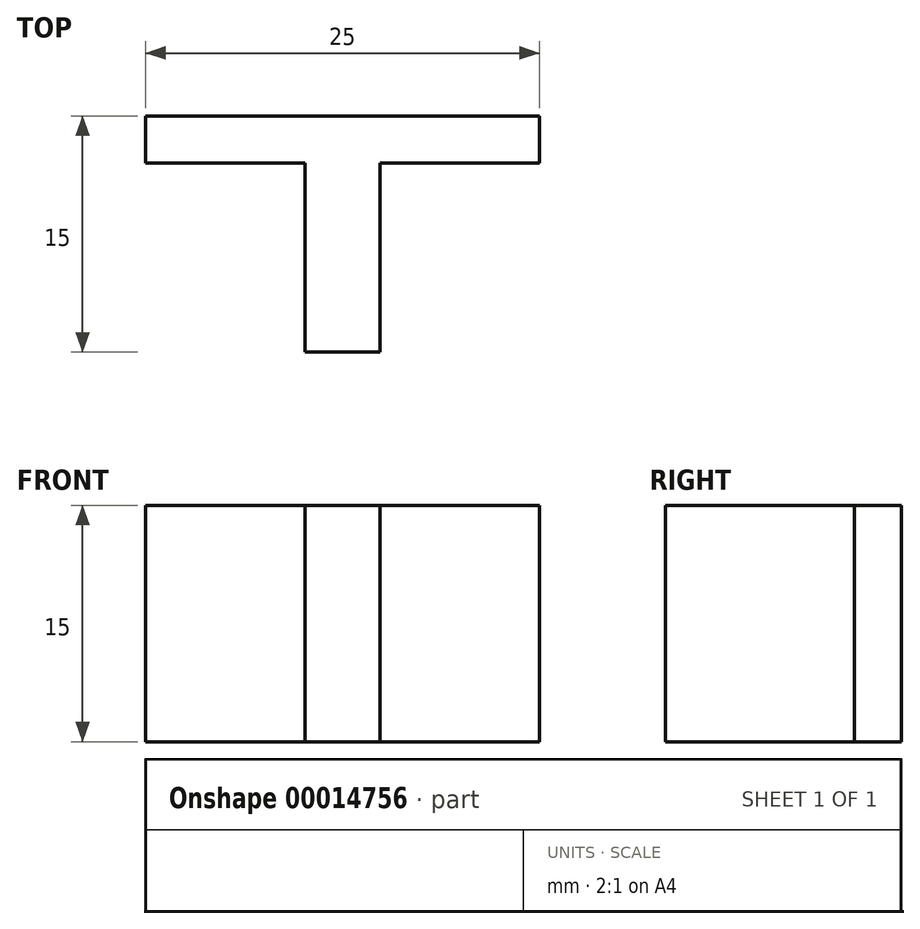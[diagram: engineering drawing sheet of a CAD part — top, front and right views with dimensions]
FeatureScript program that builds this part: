
annotation { "Feature Type Name" : "Feature", "Feature Type Description" : "" }
export const myFeature = defineFeature(function(context is Context, id is Id, definition is map)
    precondition{}
    {
        {
            var Q0;
            Q0=qCreatedBy(makeId("Top.planeOp"),FACE);
            var sketch = newSketch(context, id + "F0", { "sketchPlane" : qUnion([Q0])});
            skLineSegment(sketch, "E0", {"start": v(-12.5, 0) * mm, "end": v(-12.5, 3) * mm});
            skLineSegment(sketch, "E1", {"start": v(-12.5, 3) * mm, "end": v(12.5, 3) * mm});
            skLineSegment(sketch, "E2", {"start": v(12.5, 3) * mm, "end": v(12.5, 0) * mm});
            skLineSegment(sketch, "E3", {"start": v(12.5, 0) * mm, "end": v(2.38, 0) * mm});
            skLineSegment(sketch, "E4", {"start": v(2.37, 0) * mm, "end": v(2.38, -12) * mm});
            skLineSegment(sketch, "E5", {"start": v(2.38, -12) * mm, "end": v(-2.37, -12) * mm});
            skLineSegment(sketch, "E6", {"start": v(-2.37, -12) * mm, "end": v(-2.38, 0) * mm});
            skLineSegment(sketch, "E7", {"start": v(-2.38, 0) * mm, "end": v(-12.5, 0) * mm});
            skSolve(sketch);
        }
        {
            var Q0;
            Q0=makeQuery(id+"F0.imprint","IMPRINT",FACE,{"disambiguationData":[TD([[makeQuery(id+"F0.imprint","IMPRINT",EDGE,{"derivedFrom":sQuery(id+"F0.wireOp",EDGE,"E0")}),-1.0]])]});
            extrude(context, id + "F1", {"entities" : qUnion([Q0]), "depth" : 15 * mm});
        }
    });
